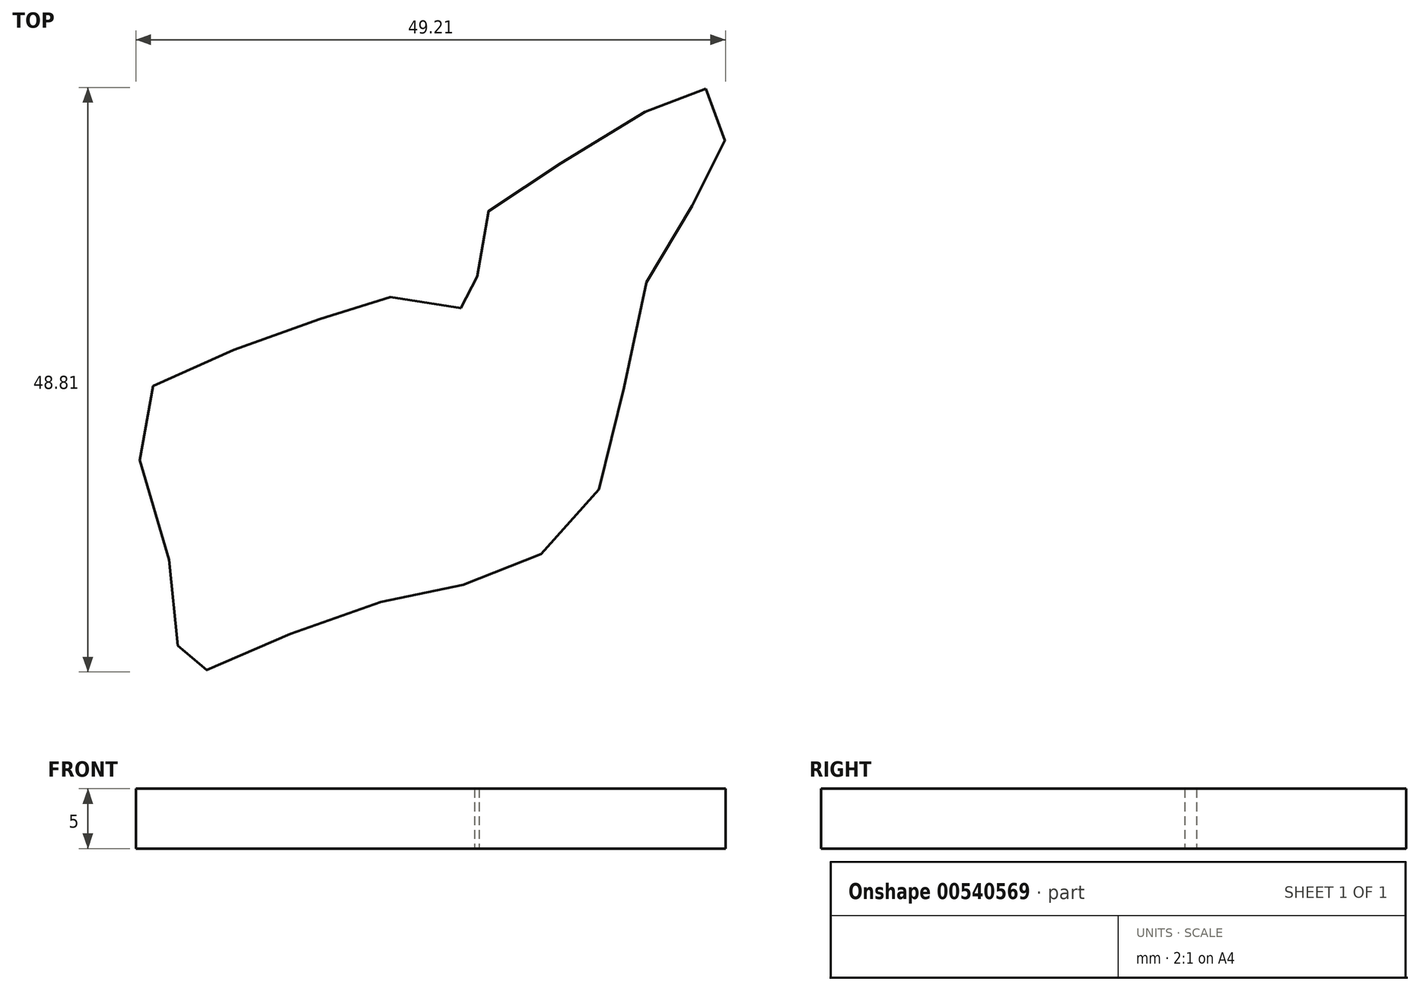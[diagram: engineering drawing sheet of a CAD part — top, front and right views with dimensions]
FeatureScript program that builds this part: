
annotation { "Feature Type Name" : "Feature", "Feature Type Description" : "" }
export const myFeature = defineFeature(function(context is Context, id is Id, definition is map)
    precondition{}
    {
        {
            var Q0;
            Q0=qCreatedBy(makeId("Top.planeOp"),FACE);
            var sketch = newSketch(context, id + "F0", { "sketchPlane" : qUnion([Q0])});
            skFitSpline(sketch, "E0", {"points": [v(19.15, 64.9) * mm, v(9.93, 60.28) * mm, v(0, 52.84) * mm, v(0, 46.8) * mm, v(-6.38, 47.52) * mm, v(-16.31, 44.33) * mm, v(-28.01, 38.65) * mm, v(-25.18, 23.4) * mm, v(-24.11, 16.31) * mm, v(-12.77, 20.57) * mm, v(0, 23.76) * mm, v(9.93, 30.85) * mm, v(14.54, 49.65) * mm, v(20.57, 59.57) * mm, v(19.15, 64.9) * mm]});
            skSolve(sketch);
        }
        {
            var Q0;
            Q0=makeQuery(id+"F0.imprint","IMPRINT",FACE,{"disambiguationData":[TD([[makeQuery(id+"F0.imprint","IMPRINT",EDGE,{"derivedFrom":sQuery(id+"F0.wireOp",EDGE,"E0")}),1.0]])]});
            extrude(context, id + "F1", {"entities" : qUnion([Q0]), "depth" : 5 * mm, "offsetDistance" : 25 * mm});
        }
    });
